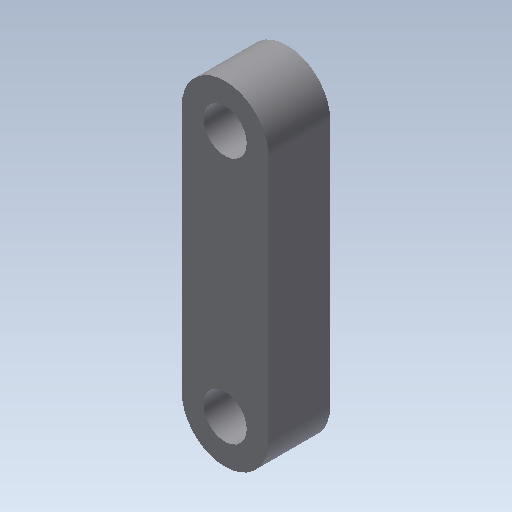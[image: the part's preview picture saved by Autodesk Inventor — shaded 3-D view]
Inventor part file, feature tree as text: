
AUTODESK INVENTOR PART (.ipt)
format: ipt  version: 2020.1 (Build 241239000, 239)  size: 100,352 bytes
history: native  units: mm
features: extrude x2, sketch x2
ambient origin geometry x8: Origin, YZ Plane, XZ Plane, XY Plane, X Axis, Y Axis, Z Axis, Center Point
bodies: Solid1 (feature_tree)
feature tree (4):
  extrude  "Extrusion1"  Depth=20.0mm
  extrude  "Extrusion2"  Depth=5.0mm TaperAngle=0.0deg
  sketch  "Sketch1"  dims[d0=7.0mm d1=20.0mm]
  sketch  "Sketch2"  dims[d2=7.0mm d3=5.0mm d4=0.0mm d5=3.5mm d6=3.5mm d7=5.0mm d8=0.0mm]
